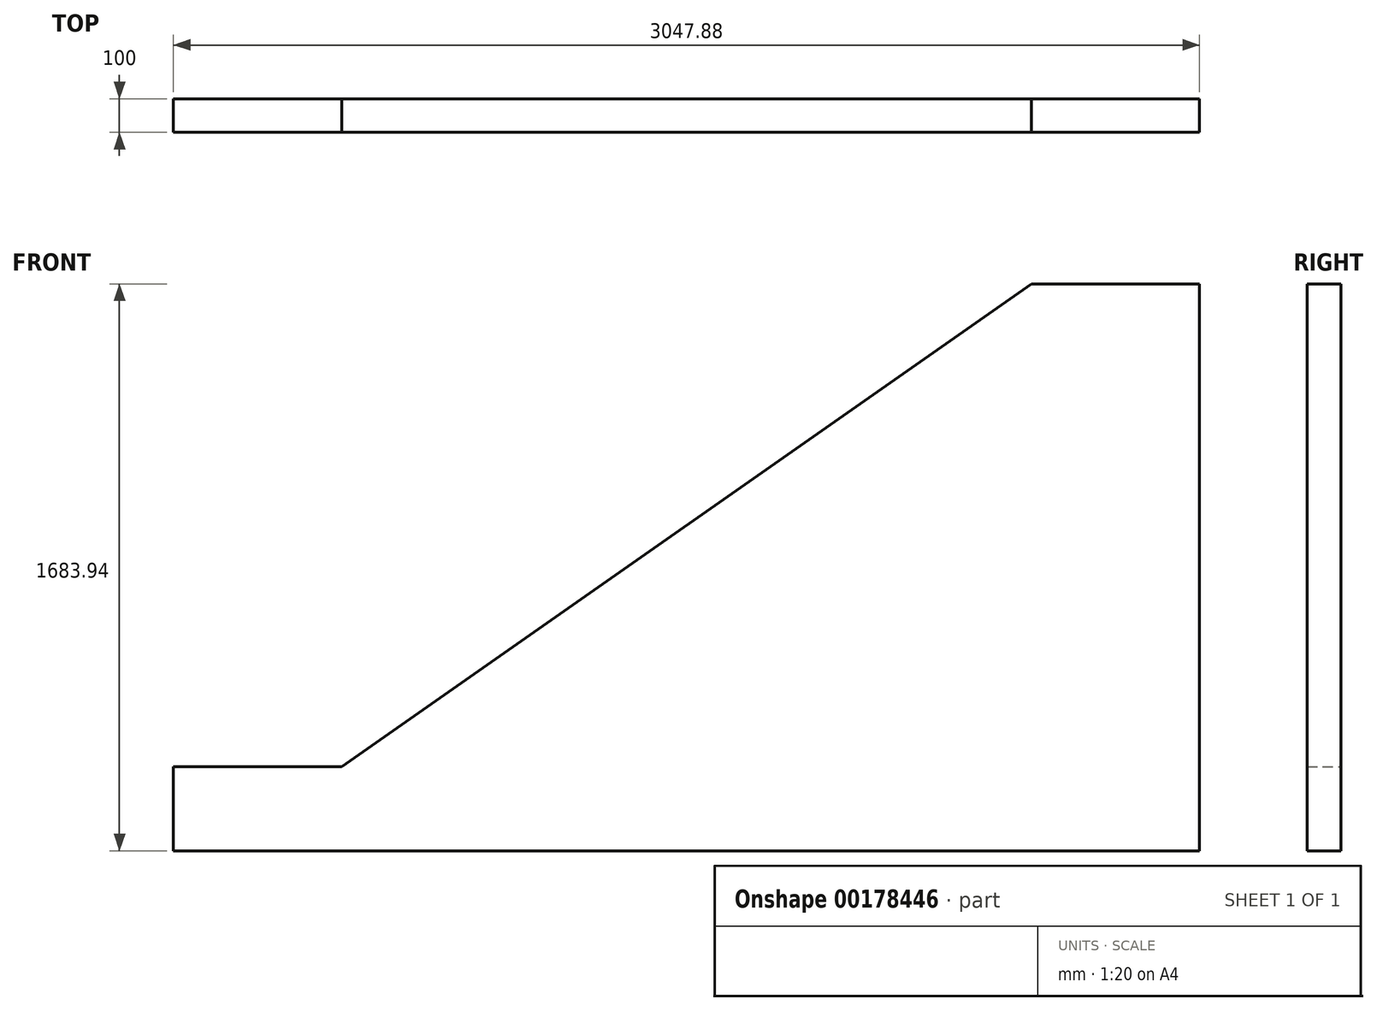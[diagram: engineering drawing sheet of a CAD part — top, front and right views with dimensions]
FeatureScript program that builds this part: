
annotation { "Feature Type Name" : "Feature", "Feature Type Description" : "" }
export const myFeature = defineFeature(function(context is Context, id is Id, definition is map)
    precondition{}
    {
        {
            var Q0;
            Q0=qCreatedBy(makeId("Front.planeOp"),FACE);
            var sketch = newSketch(context, id + "F0", { "sketchPlane" : qUnion([Q0])});
            skLineSegment(sketch, "E0", {"start": v(0, 0) * mm, "end": v(500, 0) * mm});
            skLineSegment(sketch, "E1", {"start": v(500, 0) * mm, "end": v(2547.88, 1433.94) * mm});
            skLineSegment(sketch, "E2", {"start": v(2547.88, 1433.94) * mm, "end": v(3047.88, 1433.94) * mm});
            skLineSegment(sketch, "E3", {"start": v(0, 0) * mm, "end": v(0, -250) * mm});
            skLineSegment(sketch, "E4", {"start": v(0, -250) * mm, "end": v(3047.88, -250) * mm});
            skLineSegment(sketch, "E5", {"start": v(3047.88, -250) * mm, "end": v(3047.88, 1433.94) * mm});
            skSolve(sketch);
        }
        {
            var Q0;
            Q0 = qSketchRegion(id + "F0", true);
            extrude(context, id + "F1", {"entities" : qUnion([Q0]), "depth" : 100 * mm});
        }
    });
